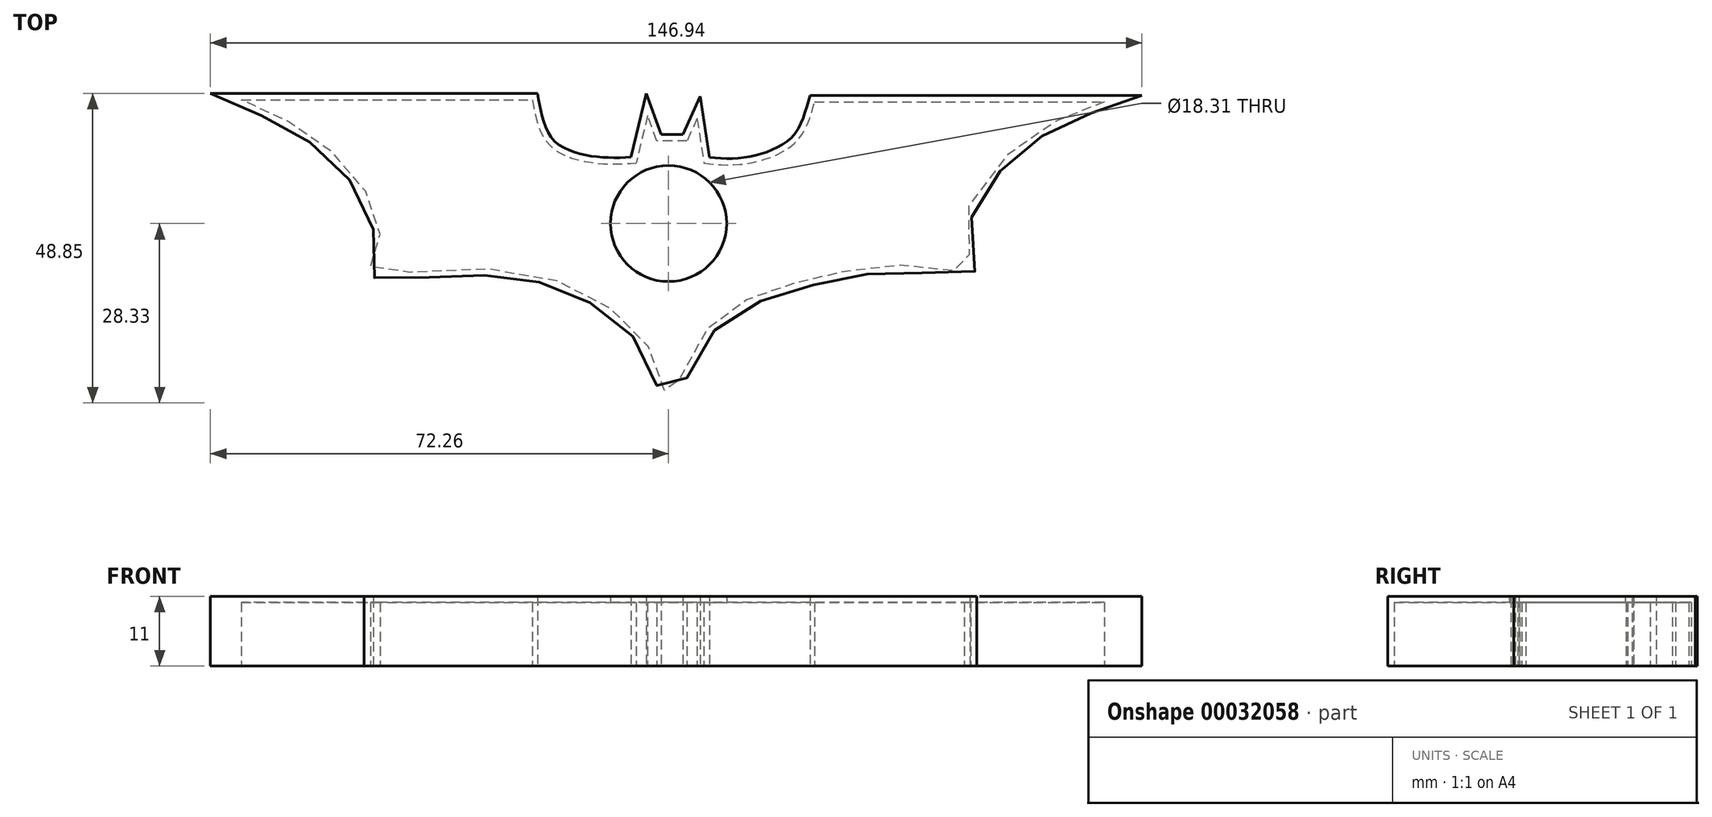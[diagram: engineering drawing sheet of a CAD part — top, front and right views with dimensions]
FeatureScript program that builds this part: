
annotation { "Feature Type Name" : "Feature", "Feature Type Description" : "" }
export const myFeature = defineFeature(function(context is Context, id is Id, definition is map)
    precondition{}
    {
        {
            var Q0;
            Q0=qCreatedBy(makeId("Top.planeOp"),FACE);
            var sketch = newSketch(context, id + "F0", { "sketchPlane" : qUnion([Q0])});
            skLineSegment(sketch, "E0", {"start": v(-67.36, 19.52) * mm, "end": v(-21.5, 19.52) * mm});
            skLineSegment(sketch, "E1", {"start": v(23.06, 19.2) * mm, "end": v(68.76, 19.2) * mm});
            skLineSegment(sketch, "E2", {"start": v(4.5, 16.57) * mm, "end": v(5.57, 9.53) * mm});
            skLineSegment(sketch, "E3", {"start": v(4.5, 16.57) * mm, "end": v(2.91, 13.05) * mm});
            skPoint(sketch, "E3.endSnap0", {"position": v(5.04, 13.05) * mm});
            skLineSegment(sketch, "E4", {"start": v(2.91, 13.05) * mm, "end": v(-1.84, 13.05) * mm});
            skLineSegment(sketch, "E5", {"start": v(-1.84, 13.05) * mm, "end": v(-3.31, 17.06) * mm});
            skLineSegment(sketch, "E6", {"start": v(-3.31, 17.06) * mm, "end": v(-5.12, 9.53) * mm});
            skFitSpline(sketch, "E7", {"points": [v(-21.5, 19.52) * mm, v(-18.71, 12.31) * mm, v(-11.34, 9.53) * mm, v(-5.12, 9.53) * mm], "startDerivative": vector(4.52, -23.84) * mm, "endDerivative": vector(19.06, 1.2) * mm});
            skPoint(sketch, "E8.2.internal.snap0", {"position": v(0.54, 13.05) * mm});
            skFitSpline(sketch, "E8", {"points": [v(5.57, 9.53) * mm, v(12.74, 9.53) * mm, v(20.27, 13.05) * mm, v(23.06, 19.2) * mm], "startDerivative": vector(22, -2.7) * mm, "endDerivative": vector(5.99, 20.43) * mm});
            skFitSpline(sketch, "E9", {"points": [v(68.76, 19.2) * mm, v(57.13, 13.79) * mm, v(46.65, 0) * mm, v(47.46, -7.02) * mm, v(39.11, -6.7) * mm, v(25.02, -8.16) * mm, v(13.72, -11.44) * mm, v(4.88, -18.32) * mm, v(0, -27.33) * mm, v(-1.84, -22.09) * mm, v(-10.36, -12.59) * mm, v(-28.87, -7.18) * mm, v(-46.89, -7.18) * mm, v(-45.74, -3.41) * mm, v(-47.7, 4.94) * mm, v(-56.71, 14.11) * mm, v(-67.36, 19.52) * mm], "startDerivative": vector(-182.09, -63.33) * mm, "endDerivative": vector(-168.66, 71.9) * mm});
            skSolve(sketch);
        }
        {
            var Q0;
            Q0=makeQuery(id+"F0.imprint","IMPRINT",FACE,{"disambiguationData":[TD([[makeQuery(id+"F0.imprint","IMPRINT",EDGE,{"derivedFrom":sQuery(id+"F0.wireOp",EDGE,"E0")}),-1.0]])]});
            extrude(context, id + "F1", {"entities" : qUnion([Q0]), "depth" : 10 * mm});
        }
        {
            var Q0;
            Q0=makeQuery(id+"F1.opExtrude","CAP_FACE",FACE,{"disambiguationData":[OSD([sQuery(id+"F0.wireOp",EDGE,"E0"),sQuery(id+"F0.wireOp",EDGE,"E1"),sQuery(id+"F0.wireOp",EDGE,"E2"),sQuery(id+"F0.wireOp",EDGE,"E3"),sQuery(id+"F0.wireOp",EDGE,"E4"),sQuery(id+"F0.wireOp",EDGE,"E5"),sQuery(id+"F0.wireOp",EDGE,"E6"),sQuery(id+"F0.wireOp",EDGE,"E7"),sQuery(id+"F0.wireOp",EDGE,"E8"),sQuery(id+"F0.wireOp",EDGE,"E9")])],"isStart":true});
            shell(context, id + "F2", {"entities" : qUnion([Q0]), "thickness" : 1 * mm, "oppositeDirection" : true});
        }
        {
            var Q0;
            Q0=makeQuery(id+"F2.opShell","OFFSET_FACE",FACE,{"disambiguationData":[OSD([sQuery(id+"F0.wireOp",EDGE,"E0"),sQuery(id+"F0.wireOp",EDGE,"E1"),sQuery(id+"F0.wireOp",EDGE,"E2"),sQuery(id+"F0.wireOp",EDGE,"E3"),sQuery(id+"F0.wireOp",EDGE,"E4"),sQuery(id+"F0.wireOp",EDGE,"E5"),sQuery(id+"F0.wireOp",EDGE,"E6"),sQuery(id+"F0.wireOp",EDGE,"E7"),sQuery(id+"F0.wireOp",EDGE,"E8"),sQuery(id+"F0.wireOp",EDGE,"E9")])]});
            var sketch = newSketch(context, id + "F3", { "sketchPlane" : qUnion([Q0])});
            skCircle(sketch, "E10", {"center": v(0, 0) * mm, "radius": 9.16 * mm});
            skSolve(sketch);
        }
        {
            var Q0;
            Q0 = qSketchRegion(id + "F3", true);
            var Q1;
            Q1=makeQuery(id+"F3.imprint","IMPRINT",FACE,{"disambiguationData":[TD([[makeQuery(id+"F3.imprint","IMPRINT",EDGE,{"derivedFrom":sQuery(id+"F3.wireOp",EDGE,"E10")}),1.0]])]});
            extrude(context, id + "F4", {"entities" : qUnion([Q0, Q1]), "operationType" : NewBodyOperationType.REMOVE, "oppositeDirection" : true, "depth" : 25.4 * mm});
        }
    });
